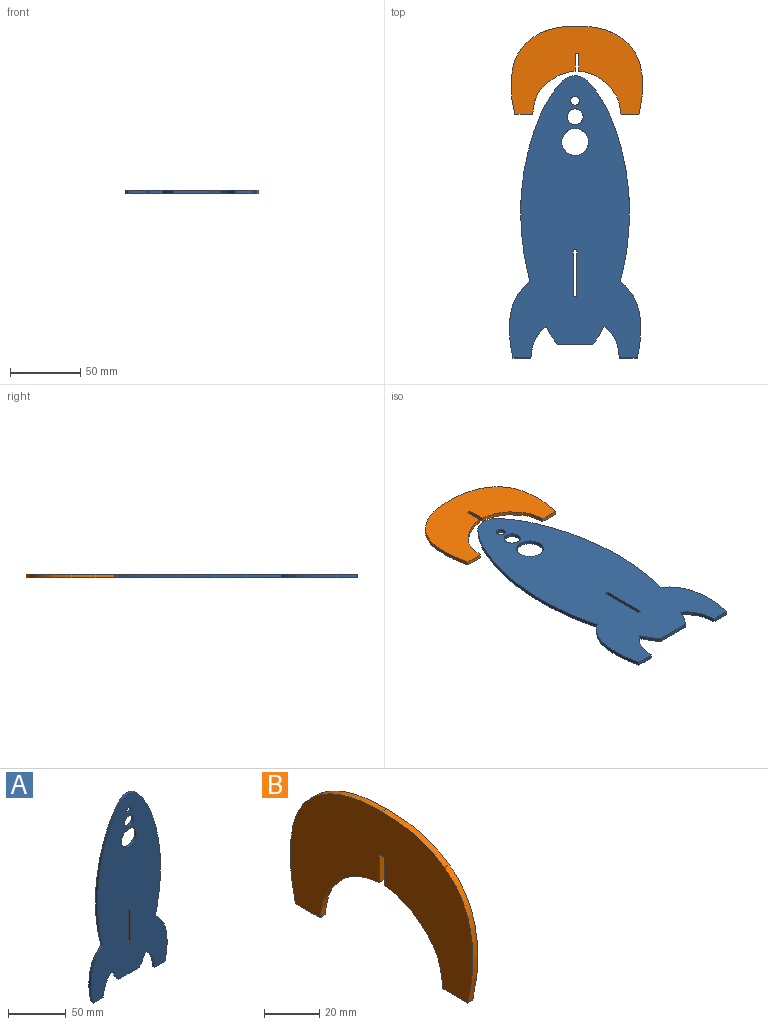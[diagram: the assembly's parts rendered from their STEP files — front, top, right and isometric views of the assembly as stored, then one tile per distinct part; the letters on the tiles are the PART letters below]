
ASSEMBLY  parts=2 mates=1
PART A: 21 faces, bbox 95.3x2.5x200.4 mm
  f0: plane 200.4x95.26mm, normal (0,-1,0), area 12643mm2, adj f2,f3,f4,f5,f6,f7,f8,f9
  f1: plane 200.4x95.26mm, normal (0,1,0), area 12643mm2, adj f2,f3,f4,f5,f6,f7,f8,f9
  f2: extruded ~142.79x29.78mm, area 381.3mm2, adj f0,f1,f3,f13
  f3: extruded ~53.99x14.65mm, area 149.4mm2, adj f0,f1,f2,f4
  f4: plane 12.7x2.54mm, normal (0,0,-1), area 32.3mm2, adj f0,f1,f3,f5
  f5: extruded ~22.58x10.85mm, area 65.9mm2, adj f0,f1,f4,f6
  f6: extruded ~13.05x7.86mm, area 38.8mm2, adj f0,f1,f5,f7
  f7: plane 25.4x2.54mm, normal (0,0,-1), area 64.5mm2, adj f0,f1,f6,f8
  f8: extruded ~13.05x7.86mm, area 38.8mm2, adj f0,f1,f7,f9
  f9: extruded ~22.58x10.85mm, area 65.9mm2, adj f0,f1,f8,f10
  f10: plane 12.7x2.54mm, normal (0,0,-1), area 32.3mm2, adj f0,f1,f9,f11
  f11: extruded ~53.99x14.65mm, area 149.4mm2, adj f0,f1,f10,f12
  f12: extruded ~142.79x29.78mm, area 381.3mm2, adj f0,f1,f11,f13
  f13: cylinder r=12.7mm len=17.75mm, axis (0,1,0), area 49.9mm2, adj f0,f1,f2,f12
  f14: plane 33.37x2.54mm, normal (-1,0,0), area 84.8mm2, adj f0,f1,f16,f17
  f15: plane 33.37x2.54mm, normal (1,0,0), area 84.8mm2, adj f0,f1,f16,f17
  f16: plane 2.54x2.54mm, normal (0,0,1), area 6.5mm2, adj f0,f1,f14,f15
  f17: plane 2.54x2.54mm, normal (0,0,-1), area 6.5mm2, adj f0,f1,f14,f15
  f18: cylinder r=3.17mm len=6.35mm, axis (0,1,0), area 50.7mm2, adj f0,f1
  f19: cylinder r=5.66mm len=11.33mm, axis (0,1,0), area 90.4mm2, adj f0,f1
  f20: cylinder r=9.53mm len=19.05mm, axis (0,1,0), area 152mm2, adj f0,f1
PART B: 15 faces, bbox 2.5x95.3x62.8 mm
  f0: extruded ~19.29x8.06mm, area 54.1mm2, adj f1,f6,f11,f13
  f1: plane 95.26x62.78mm, normal (1,0,0), area 3628.3mm2, adj f0,f2,f3,f4,f5,f6,f7,f8
  f2: extruded ~32.09x8.78mm, area 86mm2, adj f1,f3,f10,f11
  f3: extruded ~32.09x8.78mm, area 86mm2, adj f1,f2,f4,f11
  f4: extruded ~53.99x14.65mm, area 149.4mm2, adj f1,f3,f5,f11
  f5: plane 12.7x2.54mm, normal (0,0,-1), area 32.3mm2, adj f1,f4,f6,f11
  f6: extruded ~22.58x10.85mm, area 65.3mm2, adj f0,f1,f5,f11
  f7: extruded ~19.29x8.06mm, area 54.1mm2, adj f1,f8,f11,f12
  f8: extruded ~22.58x10.85mm, area 65.9mm2, adj f1,f7,f9,f11
  f9: plane 12.7x2.54mm, normal (0,0,-1), area 32.3mm2, adj f1,f8,f10,f11
  f10: extruded ~53.99x14.65mm, area 149.4mm2, adj f1,f2,f9,f11
  f11: plane 95.26x62.78mm, normal (-1,0,0), area 3628.3mm2, adj f0,f2,f3,f4,f5,f6,f7,f8
  f12: plane 12.73x2.54mm, normal (0,1,0), area 32.3mm2, adj f1,f7,f11,f14
  f13: plane 12.73x2.54mm, normal (0,-1,0), area 32.3mm2, adj f0,f1,f11,f14
  f14: plane 2.54x2.54mm, normal (0,0,-1), area 6.5mm2, adj f1,f11,f12,f13
PLACE A rot(axis=(-1,0,0),90deg) t=(0,-90.12,-1.59)mm fixed
PLACE B rot(axis=(-0.58,-0.58,-0.58),120deg) t=(1.26,82.89,-1.59)mm fixed
MATE planar B.f1 <-> A.f0  axis (0,0,1) through (1.26,126.26,-0.32)mm
